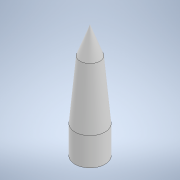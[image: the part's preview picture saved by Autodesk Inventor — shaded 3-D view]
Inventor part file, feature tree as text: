
AUTODESK INVENTOR PART (.ipt)
format: ipt  version: 2021.1 (Build 251245010, 245A)  size: 131,072 bytes
history: native  units: in
note: dims shown in document units (in); Inventor stores cm internally (conversion verified against a paired STEP export)
features: revolve x1, sketch x1
ambient origin geometry x8: Origin, YZ Plane, XZ Plane, XY Plane, X Axis, Y Axis, Z Axis, Center Point
bodies: Solid1 (feature_tree)
feature tree (2):
  revolve  "Revolution1"  [1 undecoded]
  sketch  "Sketch2"  dims[d6=0.21in d7=0.16in d8=0.85in d9=0.0875in d10=0.375in d11=0.05in d13=0.1374in d14=0.0312in d15=90.0deg]
note: 1 required parameter value undecoded (feature->parameter linkage not recoverable at this tier; creation-order binding heuristic only, values carry confidence <= 0.55)
